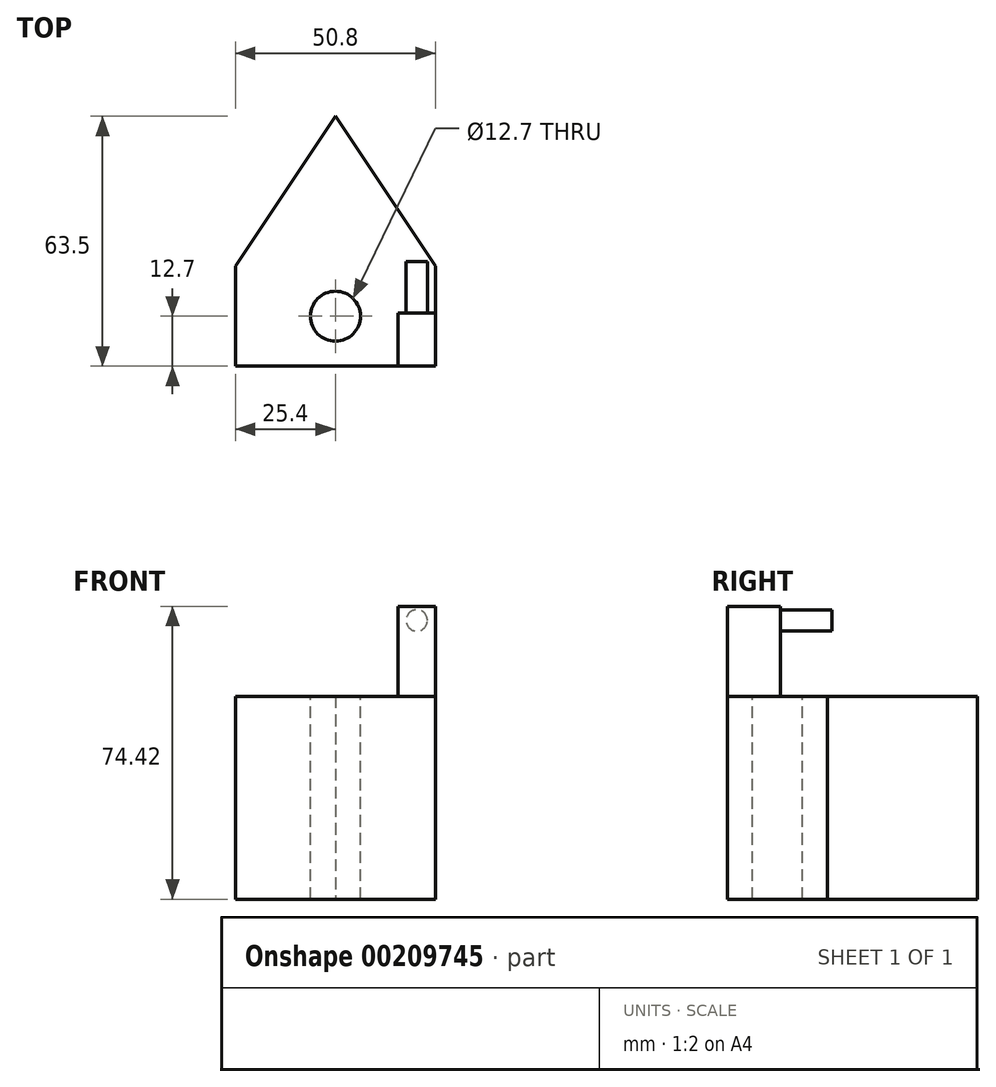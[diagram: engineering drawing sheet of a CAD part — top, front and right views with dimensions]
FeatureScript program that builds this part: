
annotation { "Feature Type Name" : "Feature", "Feature Type Description" : "" }
export const myFeature = defineFeature(function(context is Context, id is Id, definition is map)
    precondition{}
    {
        {
            var Q0;
            Q0=qCreatedBy(makeId("Top.planeOp"),FACE);
            var sketch = newSketch(context, id + "F0", { "sketchPlane" : qUnion([Q0])});
            skLineSegment(sketch, "E0.bottom", {"start": v(0, 0) * mm, "end": v(50.8, 0) * mm});
            skLineSegment(sketch, "E0.top", {"start": v(0, 25.4) * mm, "end": v(50.8, 25.4) * mm});
            skLineSegment(sketch, "E0.left", {"start": v(0, 0) * mm, "end": v(0, 25.4) * mm});
            skLineSegment(sketch, "E0.right", {"start": v(50.8, 0) * mm, "end": v(50.8, 25.4) * mm});
            skPoint(sketch, "E1", {"position": v(50.8, 25.4) * mm});
            skPoint(sketch, "E2", {"position": v(25.4, 25.4) * mm});
            skLineSegment(sketch, "E3", {"start": v(25.4, 25.4) * mm, "end": v(25.4, 63.5) * mm});
            skLineSegment(sketch, "E4", {"start": v(50.8, 25.4) * mm, "end": v(25.4, 63.5) * mm});
            skLineSegment(sketch, "E5", {"start": v(25.4, 63.5) * mm, "end": v(0, 25.4) * mm});
            skSolve(sketch);
        }
        {
            var Q0;
            Q0=makeQuery(id+"F0.imprint","IMPRINT",FACE,{"disambiguationData":[TD([[makeQuery(id+"F0.imprint","IMPRINT",EDGE,{"derivedFrom":sQuery(id+"F0.wireOp",EDGE,"E0.bottom")}),1.0]])]});
            var Q1;
            {var subQ2=sQuery(id+"F0.wireOp",EDGE,"E3");Q1=makeQuery(id+"F0.imprint","IMPRINT",FACE,{"disambiguationData":[TD([[makeQuery(id+"F0.imprint","IMPRINT",EDGE,{"derivedFrom":subQ2}),1.0]])]});}
            var Q2;
            {var subQ2=sQuery(id+"F0.wireOp",EDGE,"E3");Q2=makeQuery(id+"F0.imprint","IMPRINT",FACE,{"disambiguationData":[TD([[makeQuery(id+"F0.imprint","IMPRINT",EDGE,{"derivedFrom":subQ2}),-1.0]])]});}
            extrude(context, id + "F1", {"entities" : qUnion([Q0, Q1, Q2]), "depth" : 51.56 * mm});
        }
        {
            var Q0;
            Q0=makeQuery(id+"F1.opExtrude","CAP_FACE",FACE,{"disambiguationData":[OSD([sQuery(id+"F0.wireOp",EDGE,"E0.bottom"),sQuery(id+"F0.wireOp",EDGE,"E0.left"),sQuery(id+"F0.wireOp",EDGE,"E0.right"),sQuery(id+"F0.wireOp",EDGE,"E4"),sQuery(id+"F0.wireOp",EDGE,"E5")])],"isStart":false});
            var sketch = newSketch(context, id + "F2", { "sketchPlane" : qUnion([Q0])});
            skLineSegment(sketch, "E6", {"start": v(0, 25.4) * mm, "end": v(50.8, 0) * mm, "construction": true});
            skLineSegment(sketch, "E7", {"start": v(50.8, 0) * mm, "end": v(50.8, 25.4) * mm});
            skLineSegment(sketch, "E8", {"start": v(0, 0) * mm, "end": v(50.8, 25.4) * mm, "construction": true});
            skPoint(sketch, "E9", {"position": v(25.4, 12.7) * mm});
            skCircle(sketch, "E10", {"center": v(25.4, 12.7) * mm, "radius": 6.35 * mm});
            skSolve(sketch);
        }
        {
            var Q0;
            Q0 = qSketchRegion(id + "F2", true);
            extrude(context, id + "F3", {"entities" : qUnion([Q0]), "operationType" : NewBodyOperationType.REMOVE, "endBound" : BoundingType.THROUGH_ALL, "oppositeDirection" : true, "depth" : 25.4 * mm});
        }
        {
            var Q0;
            Q0=makeQuery(id+"F1.opExtrude","CAP_FACE",FACE,{"disambiguationData":[OSD([sQuery(id+"F0.wireOp",EDGE,"E0.bottom"),sQuery(id+"F0.wireOp",EDGE,"E0.left"),sQuery(id+"F0.wireOp",EDGE,"E0.right"),sQuery(id+"F0.wireOp",EDGE,"E4"),sQuery(id+"F0.wireOp",EDGE,"E5")])],"isStart":false});
            var sketch = newSketch(context, id + "F4", { "sketchPlane" : qUnion([Q0])});
            skLineSegment(sketch, "E11.bottom", {"start": v(50.8, 0) * mm, "end": v(41.35, 0) * mm});
            skLineSegment(sketch, "E11.top", {"start": v(50.8, 13.5) * mm, "end": v(41.35, 13.5) * mm});
            skLineSegment(sketch, "E11.left", {"start": v(50.8, 0) * mm, "end": v(50.8, 13.5) * mm});
            skLineSegment(sketch, "E11.right", {"start": v(41.35, 0) * mm, "end": v(41.35, 13.5) * mm});
            skSolve(sketch);
        }
        {
            var Q0;
            Q0 = qSketchRegion(id + "F4", true);
            extrude(context, id + "F5", {"entities" : qUnion([Q0]), "depth" : 22.86 * mm});
        }
        {
            var Q0;
            Q0=makeQuery(id+"F5.opExtrude","SWEPT_FACE",FACE,{"disambiguationData":[OSD([sQuery(id+"F4.wireOp",EDGE,"E11.top")])]});
            var sketch = newSketch(context, id + "F6", { "sketchPlane" : qUnion([Q0])});
            skLineSegment(sketch, "E12", {"start": v(-41.35, 74.42) * mm, "end": v(-41.35, 67.25) * mm});
            skLineSegment(sketch, "E13", {"start": v(-41.35, 67.25) * mm, "end": v(-50.8, 67.25) * mm, "construction": true});
            skLineSegment(sketch, "E14", {"start": v(-41.35, 74.42) * mm, "end": v(-50.8, 67.25) * mm, "construction": true});
            skLineSegment(sketch, "E15", {"start": v(-41.35, 67.25) * mm, "end": v(-50.8, 74.42) * mm, "construction": true});
            skPoint(sketch, "E16", {"position": v(-46.07, 70.83) * mm});
            skCircle(sketch, "E17", {"center": v(-46.07, 70.83) * mm, "radius": 2.7 * mm});
            skSolve(sketch);
        }
        {
            var Q0;
            Q0=makeQuery(id+"F6.imprint","IMPRINT",FACE,{"disambiguationData":[TD([[makeQuery(id+"F6.imprint","IMPRINT",EDGE,{"derivedFrom":sQuery(id+"F6.wireOp",EDGE,"E17")}),1.0]])]});
            extrude(context, id + "F7", {"entities" : qUnion([Q0]), "operationType" : NewBodyOperationType.ADD, "depth" : 13.06 * mm});
        }
    });
